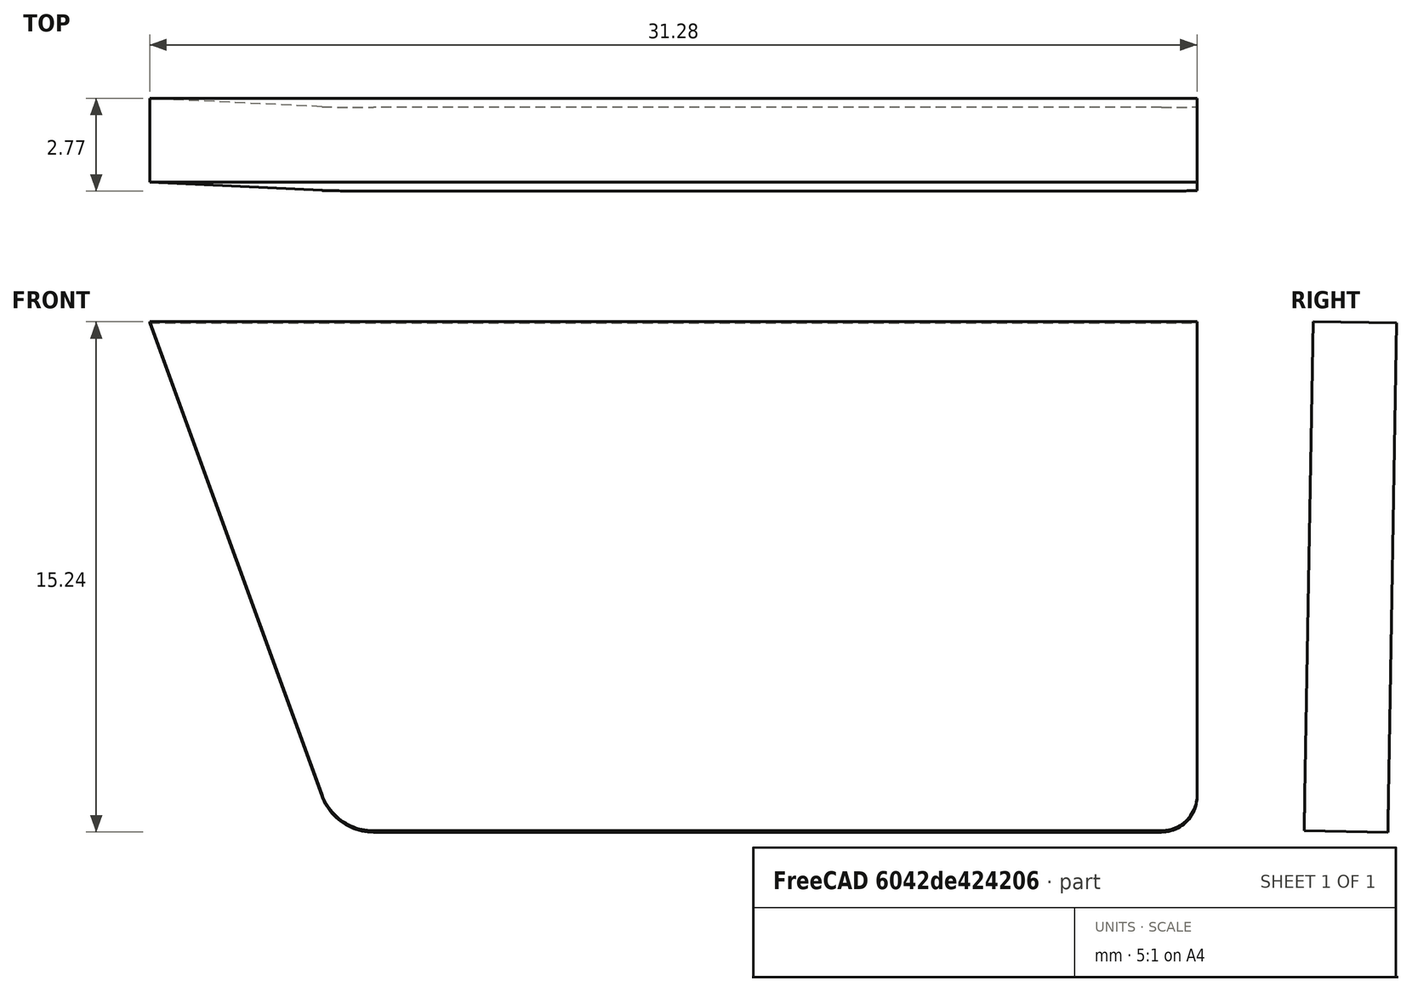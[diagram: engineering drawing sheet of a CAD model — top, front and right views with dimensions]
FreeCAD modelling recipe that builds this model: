
FCSTD DOCUMENT  (FreeCAD 0.16R6700 (Git))
Label: Magazine Bumper Pad 15mm - v2 - Corte Esq
License: FreeArt
LicenseURL: http://artlibre.org/licence/lal
objects: Sketcher::SketchObject×1, PartDesign::Pad×1
note: 3 computed .brp shape members not serialized (recipe doc carries the construction recipe); baked Part::Feature solids carry a one-line shape summary decoded from their .brp

FEATURE [Sketcher::SketchObject] Sketch005
  Placement = pos=(0,6.3,0) rot=(1,0,0;1.55334rad)
  sketch-geometry (6):
    g0: LineSegment StartX=-17.2882 StartY=3.81376 StartZ=0 EndX=13.9901 EndY=3.81376 EndZ=0
    g1: LineSegment StartX=13.9901 StartY=3.81376 StartZ=0 EndX=13.9901 EndY=-10.3321 EndZ=0
    g2: LineSegment StartX=12.9273 StartY=-11.3949 StartZ=0 EndX=-10.6085 EndY=-11.3949 EndZ=0
    g3: LineSegment StartX=-12.1441 StartY=-10.3197 StartZ=0 EndX=-17.2882 EndY=3.81376 EndZ=0
    g4: ArcOfCircle CenterX=-10.6085 CenterY=-9.76078 CenterZ=0 NormalX=0 NormalY=0 NormalZ=1 Radius=1.63408 StartAngle=3.49066 EndAngle=4.71239
    g5: ArcOfCircle CenterX=12.9273 CenterY=-10.3321 CenterZ=0 NormalX=0 NormalY=0 NormalZ=1 Radius=1.06278 StartAngle=4.71239 EndAngle=6.28319
  constraints (10):
    c: Coincident(g0,g1)
    c: Coincident(g3,g0)
    c: Horizontal(g0)
    c: Horizontal(g2)
    c: Vertical(g1)
    c: Tangent(g3,g4) = 1.5708
    c: Tangent(g2,g4) = 1.5708
    c: Tangent(g2,g5) = 1.5708
    c: Tangent(g1,g5) = 1.5708
    c: Angle(g2,g3) = 1.91986
FEATURE [PartDesign::Pad] Pad001  label="Corte da Esquerda"
  Length = 2.5
  Length2 = 100
  Midplane = true
  Placement = pos=(0,6.3,0) rot=(1,0,0;1.55334rad)
  Sketch = -> Sketch005
  Type = 0
